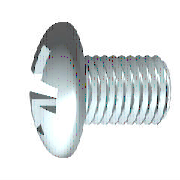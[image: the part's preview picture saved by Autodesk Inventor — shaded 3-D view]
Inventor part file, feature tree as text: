
AUTODESK INVENTOR PART (.ipt)
format: ipt  version: 2019 (Build 230136000, 136)  size: 274,944 bytes
history: native  units: mm (DEFAULTED — no unit token found)
features: other x2, plane x2, extrude x1
ambient origin geometry x7: Origin, YZ Plane, XZ Plane, X Axis, Y Axis, Z Axis, Center Point
bodies: Solid1 (feature_tree)
feature tree (5):
  other  "Cuerpo"
  plane  "Work Plane1"
  extrude  "Ranura"  Depth=4.0mm
  other  "Corte"
  plane  "Work Plane3"
